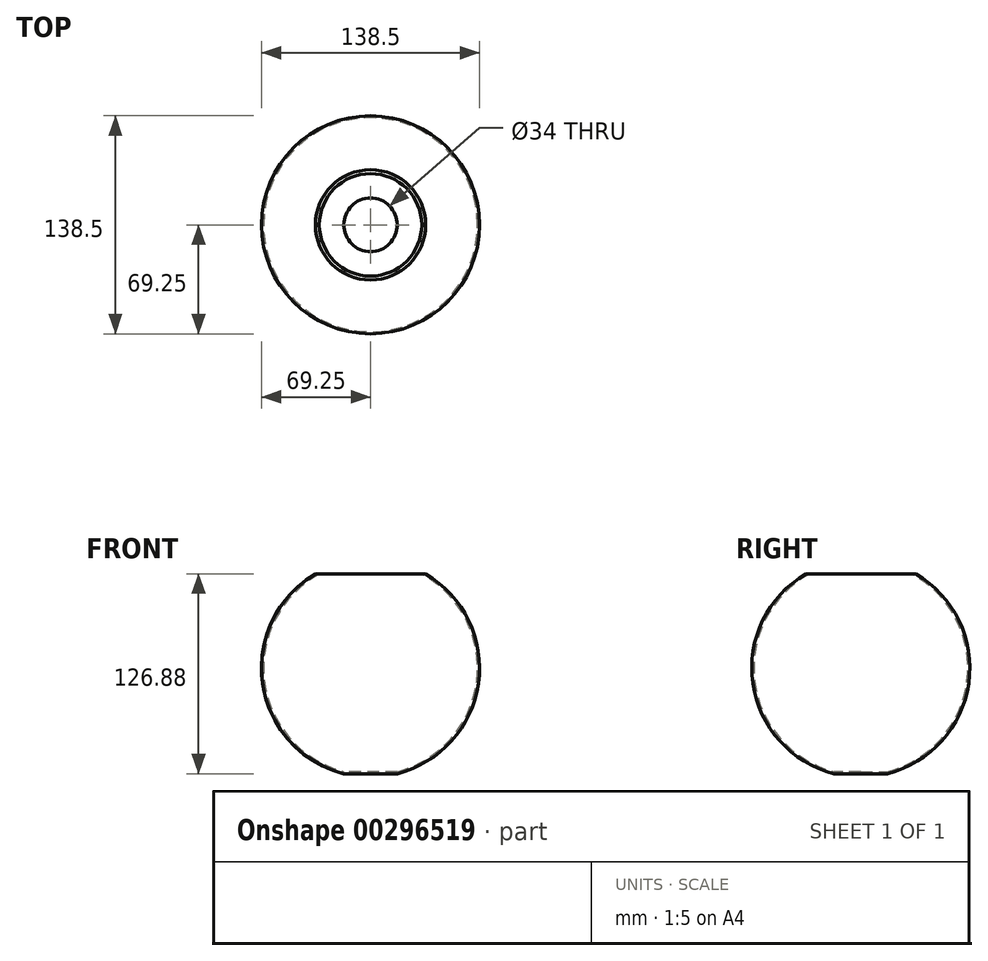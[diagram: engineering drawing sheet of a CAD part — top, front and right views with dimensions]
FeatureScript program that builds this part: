
annotation { "Feature Type Name" : "Feature", "Feature Type Description" : "" }
export const myFeature = defineFeature(function(context is Context, id is Id, definition is map)
    precondition{}
    {
        {
            var Q0;
            Q0=qCreatedBy(makeId("Front.planeOp"),FACE);
            var sketch = newSketch(context, id + "F0", { "sketchPlane" : qUnion([Q0])});
            skLineSegment(sketch, "E0", {"start": v(0, 0) * mm, "end": v(-16.5, 0) * mm});
            skLineSegment(sketch, "E1", {"start": v(0, 0) * mm, "end": v(0, 127) * mm});
            skLineSegment(sketch, "E2", {"start": v(0, 127) * mm, "end": v(-35, 127) * mm});
            skArc(sketch, "E3", {"start": v(-35, 127) * mm, "mid": v(-68.52, 57.27) * mm, "end": v(-16.5, 0) * mm});
            skSolve(sketch);
        }
        {
            var Q0;
            Q0 = qSketchRegion(id + "F0", true);
            var Q1;
            Q1=sQuery(id+"F0.wireOp",EDGE,"E1");
            revolve(context, id + "F1", {"entities" : qUnion([Q0]), "axis" : qUnion([Q1]), "revolveType" : RevolveType.FULL});
        }
        {
            var Q0;
            Q0=makeQuery(id+"F1.opRevolve","SWEPT_FACE",FACE,{"disambiguationData":[OSD([sQuery(id+"F0.wireOp",EDGE,"E2")])]});
            shell(context, id + "F2", {"entities" : qUnion([Q0]), "thickness" : 1.2 * mm});
        }
        {
            var Q0;
            Q0=makeQuery(id+"F2.opShell","OFFSET_FACE",FACE,{"disambiguationData":[OSD([sQuery(id+"F0.wireOp",EDGE,"E0")])]});
            var sketch = newSketch(context, id + "F3", { "sketchPlane" : qUnion([Q0])});
            skCircle(sketch, "E4", {"center": v(0, 0) * mm, "radius": 17 * mm});
            skSolve(sketch);
        }
        {
            var Q0;
            Q0 = qSketchRegion(id + "F3", true);
            extrude(context, id + "F4", {"entities" : qUnion([Q0]), "operationType" : NewBodyOperationType.REMOVE, "oppositeDirection" : true, "depth" : 25 * mm, "hasSecondDirection" : true, "secondDirectionOppositeDirection" : false, "secondDirectionDepth" : 25 * mm});
        }
    });
